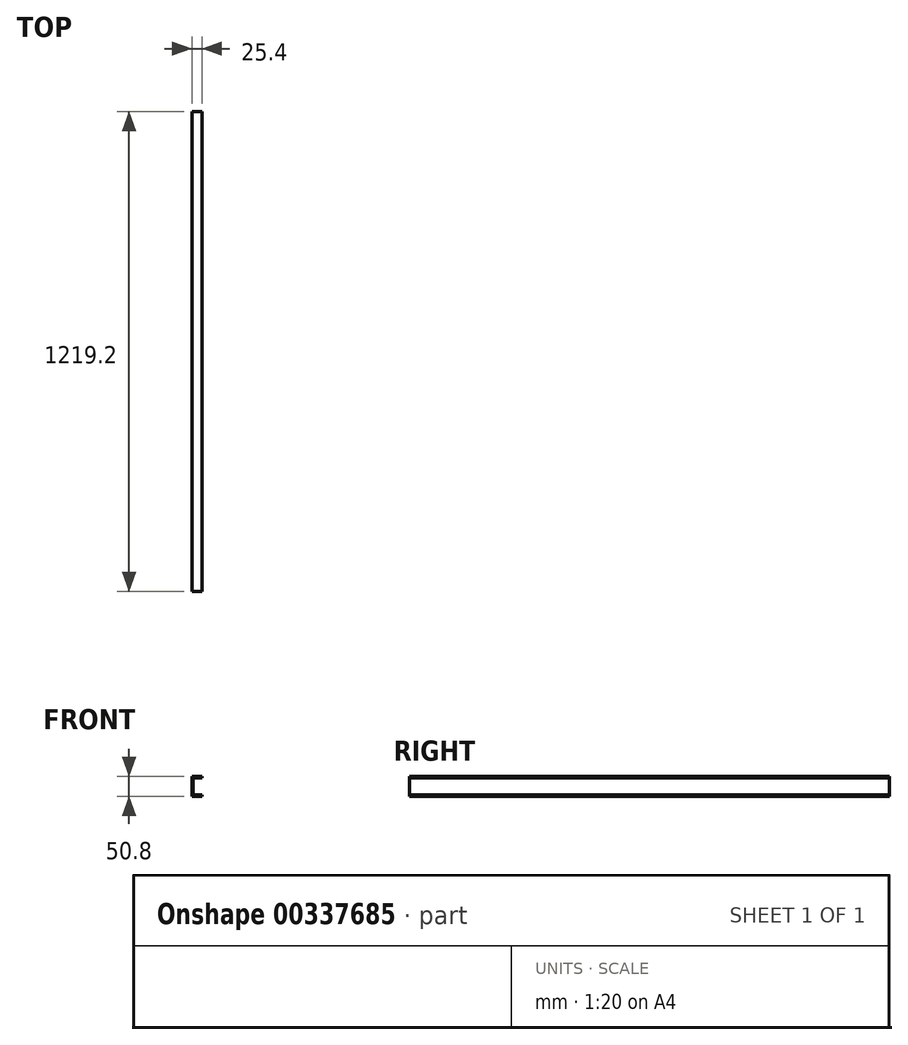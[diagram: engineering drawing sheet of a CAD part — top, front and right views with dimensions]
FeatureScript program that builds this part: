
annotation { "Feature Type Name" : "Feature", "Feature Type Description" : "" }
export const myFeature = defineFeature(function(context is Context, id is Id, definition is map)
    precondition{}
    {
        {
            var Q0;
            Q0=qCreatedBy(makeId("Front.planeOp"),FACE);
            var sketch = newSketch(context, id + "F0", { "sketchPlane" : qUnion([Q0])});
            skLineSegment(sketch, "E0.bottom", {"start": v(0, 0) * mm, "end": v(25.4, 0) * mm});
            skLineSegment(sketch, "E0.top", {"start": v(0, 50.8) * mm, "end": v(25.4, 50.8) * mm});
            skLineSegment(sketch, "E0.left", {"start": v(0, 0) * mm, "end": v(0, 50.8) * mm});
            skLineSegment(sketch, "E1.0", {"start": v(3.3, 3.3) * mm, "end": v(25.4, 3.3) * mm});
            skLineSegment(sketch, "E1.1", {"start": v(3.3, 3.3) * mm, "end": v(3.3, 47.5) * mm});
            skLineSegment(sketch, "E1.2", {"start": v(3.3, 47.5) * mm, "end": v(25.4, 47.5) * mm});
            skLineSegment(sketch, "E2", {"start": v(25.4, 0) * mm, "end": v(25.4, 3.3) * mm});
            skLineSegment(sketch, "E3.trimOffspring", {"start": v(25.4, 47.5) * mm, "end": v(25.4, 50.8) * mm});
            skPoint(sketch, "E0.right.end.orphan", {"position": v(50.8, 50.8) * mm});
            skPoint(sketch, "E4.orphan", {"position": v(50.8, 0) * mm});
            skSolve(sketch);
        }
        {
            var Q0;
            Q0 = qSketchRegion(id + "F0", true);
            extrude(context, id + "F1", {"entities" : qUnion([Q0]), "depth" : 1219.2 * mm});
        }
    });
